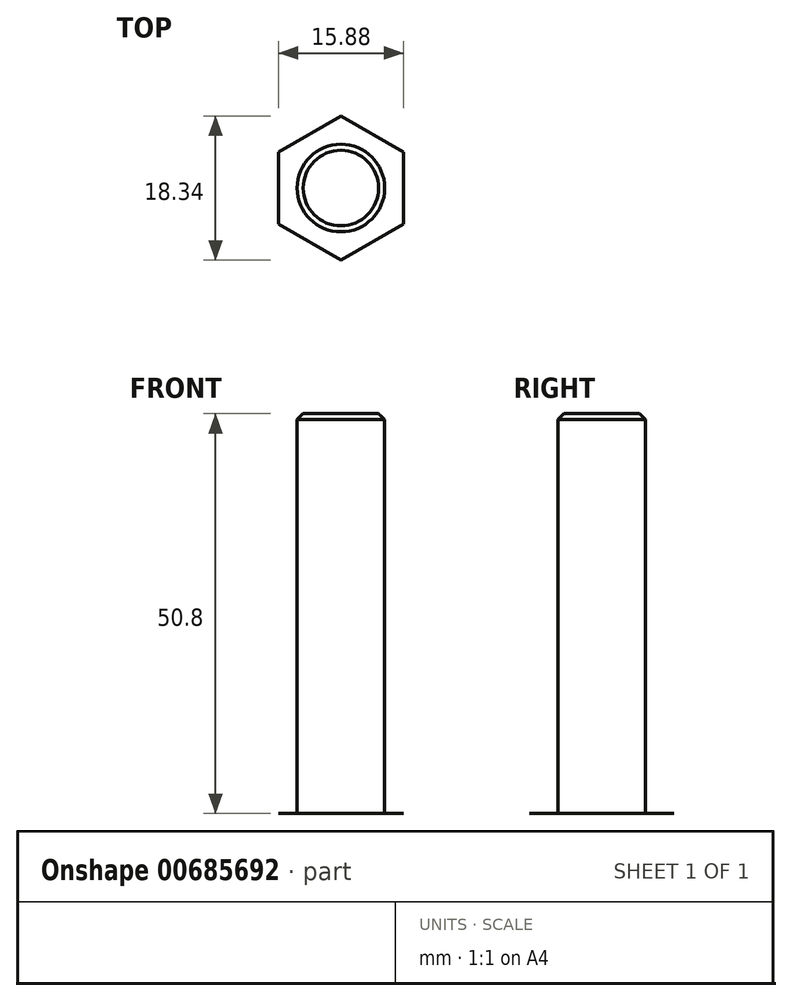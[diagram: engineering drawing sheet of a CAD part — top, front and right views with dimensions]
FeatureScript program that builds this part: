
annotation { "Feature Type Name" : "Feature", "Feature Type Description" : "" }
export const myFeature = defineFeature(function(context is Context, id is Id, definition is map)
    precondition{}
    {
        {
            var Q0;
            Q0=qCreatedBy(makeId("Top.planeOp"),FACE);
            var sketch = newSketch(context, id + "F0", { "sketchPlane" : qUnion([Q0])});
            skCircle(sketch, "E0", {"center": v(0, 0) * mm, "radius": 5.56 * mm});
            skSolve(sketch);
        }
        {
            var Q0;
            Q0=qCreatedBy(makeId("Top.planeOp"),FACE);
            var sketch = newSketch(context, id + "F1", { "sketchPlane" : qUnion([Q0])});
            skCircle(sketch, "E1.cCircle", {"center": v(0, 0) * mm, "radius": 9.17 * mm, "construction": true});
            skLineSegment(sketch, "E1.0", {"start": v(0, 9.17) * mm, "end": v(7.94, 4.58) * mm});
            skLineSegment(sketch, "E1.1", {"start": v(7.94, 4.58) * mm, "end": v(7.94, -4.58) * mm});
            skLineSegment(sketch, "E1.2", {"start": v(7.94, -4.58) * mm, "end": v(0, -9.17) * mm});
            skLineSegment(sketch, "E1.3", {"start": v(0, -9.17) * mm, "end": v(-7.94, -4.58) * mm});
            skLineSegment(sketch, "E1.4", {"start": v(-7.94, -4.58) * mm, "end": v(-7.94, 4.58) * mm});
            skLineSegment(sketch, "E1.5", {"start": v(-7.94, 4.58) * mm, "end": v(0, 9.17) * mm});
            skSolve(sketch);
        }
        {
            var Q0;
            Q0=makeQuery(id+"F1.imprint","IMPRINT",FACE,{"disambiguationData":[TD([[makeQuery(id+"F1.imprint","IMPRINT",EDGE,{"derivedFrom":sQuery(id+"F1.wireOp",EDGE,"E1.0")}),-1.0]])]});
            extrude(context, id + "F2", {"entities" : qUnion([Q0]), "depth" : 9 / 812.8 * mm, "offsetDistance" : 25.4 * mm});
        }
        {
            var Q0;
            Q0=makeQuery(id+"F0.imprint","IMPRINT",FACE,{"disambiguationData":[TD([[makeQuery(id+"F0.imprint","IMPRINT",EDGE,{"derivedFrom":sQuery(id+"F0.wireOp",EDGE,"E0")}),1.0]])]});
            extrude(context, id + "F3", {"entities" : qUnion([Q0]), "operationType" : NewBodyOperationType.ADD, "depth" : 50.8 * mm, "offsetDistance" : 25.4 * mm});
        }
        {
            var Q0;
            Q0=makeQuery(id+"F3.opExtrude","CAP_FACE",FACE,{"disambiguationData":[OSD([sQuery(id+"F0.wireOp",EDGE,"E0")])],"isStart":false});
            var sketch = newSketch(context, id + "F4", { "sketchPlane" : qUnion([Q0])});
            skCircle(sketch, "E2", {"center": v(0, 0) * mm, "radius": 5.56 * mm});
            skSolve(sketch);
        }
        {
            var Q0;
            Q0=makeQuery(id+"F3.opExtrude","CAP_EDGE",EDGE,{"disambiguationData":[OSD([sQuery(id+"F0.wireOp",EDGE,"E0")])],"isStart":false});
            chamfer(context, id + "F5", {"entities" : qUnion([Q0]), "width" : 0.76 * mm, "tangentPropagation" : true});
        }
    });
